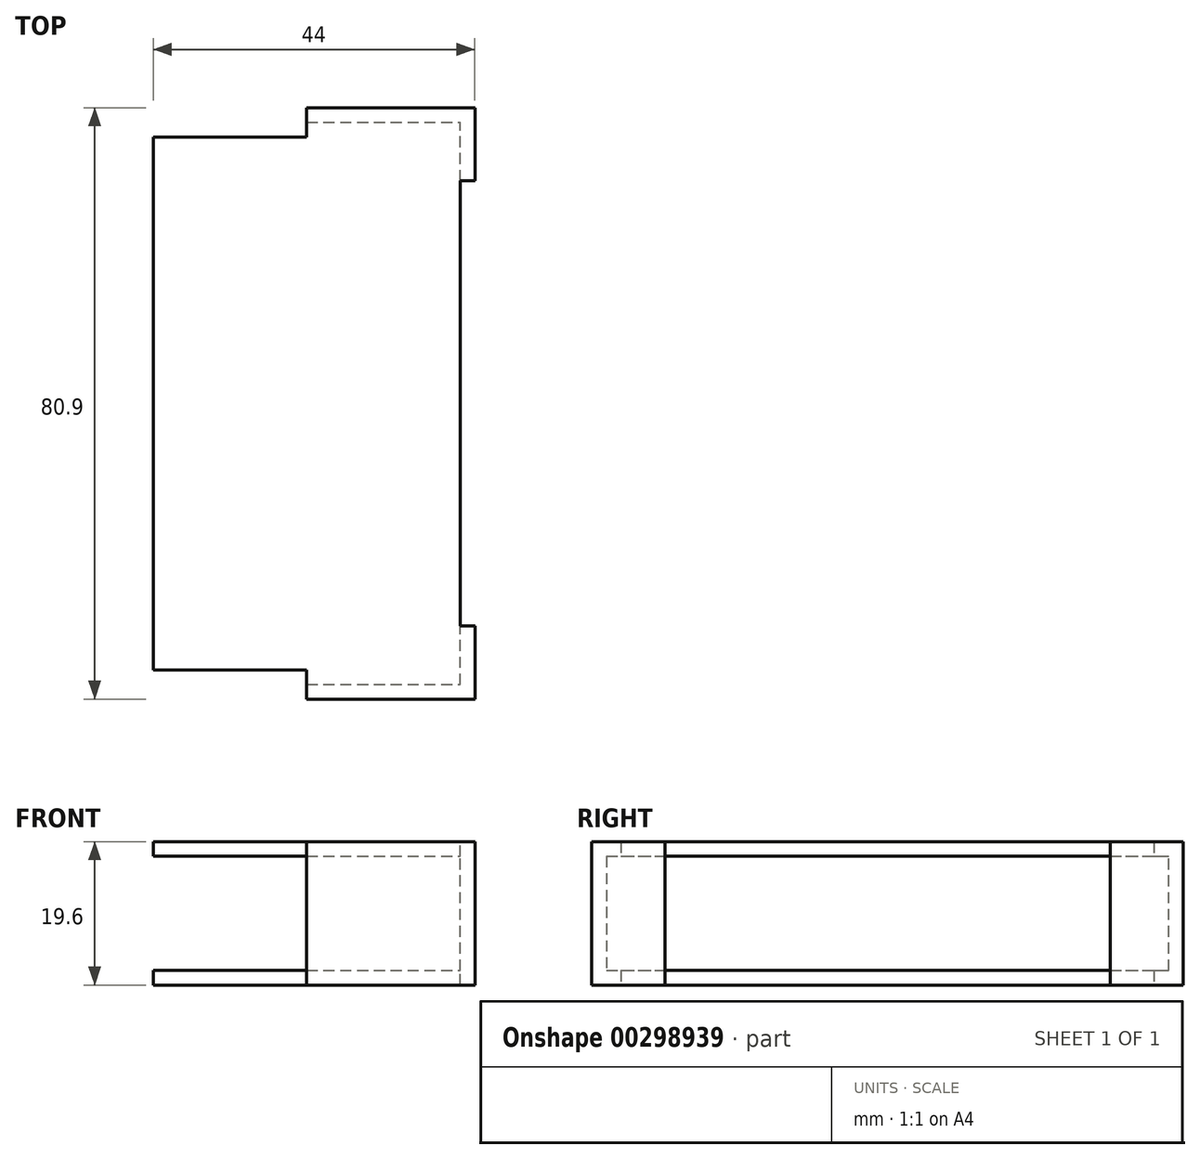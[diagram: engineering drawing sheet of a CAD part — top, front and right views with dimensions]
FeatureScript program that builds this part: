
annotation { "Feature Type Name" : "Feature", "Feature Type Description" : "" }
export const myFeature = defineFeature(function(context is Context, id is Id, definition is map)
    precondition{}
    {
        {
            var Q0;
            Q0=qCreatedBy(makeId("Front.planeOp"),FACE);
            var sketch = newSketch(context, id + "F0", { "sketchPlane" : qUnion([Q0])});
            skLineSegment(sketch, "E0.bottom", {"start": v(-6.87, 0) * mm, "end": v(11.13, 0) * mm});
            skLineSegment(sketch, "E0.top", {"start": v(-6.87, 15.6) * mm, "end": v(11.13, 15.6) * mm});
            skLineSegment(sketch, "E0.left", {"start": v(-6.87, 0) * mm, "end": v(-6.87, 15.6) * mm});
            skLineSegment(sketch, "E0.right", {"start": v(11.13, 0) * mm, "end": v(11.13, 15.6) * mm});
            skLineSegment(sketch, "E1.top", {"start": v(-6.87, 17.6) * mm, "end": v(11.13, 17.6) * mm});
            skLineSegment(sketch, "E1.left", {"start": v(-6.87, 15.6) * mm, "end": v(-6.87, 17.6) * mm});
            skLineSegment(sketch, "E1.right", {"start": v(11.13, 15.6) * mm, "end": v(11.13, 17.6) * mm});
            skLineSegment(sketch, "E2.top", {"start": v(-6.87, -2) * mm, "end": v(11.13, -2) * mm});
            skLineSegment(sketch, "E2.left", {"start": v(-6.87, 0) * mm, "end": v(-6.87, -2) * mm});
            skLineSegment(sketch, "E2.right", {"start": v(11.13, 0) * mm, "end": v(11.13, -2) * mm});
            skSolve(sketch);
        }
        {
            var Q0;
            Q0 = qSketchRegion(id + "F0", true);
            extrude(context, id + "F1", {"entities" : qUnion([Q0]), "depth" : 2 * mm});
        }
        {
            var Q0;
            Q0=makeQuery(id+"F1.opExtrude","CAP_FACE",FACE,{"disambiguationData":[OSD([sQuery(id+"F0.wireOp",EDGE,"E0.left"),sQuery(id+"F0.wireOp",EDGE,"E0.right"),sQuery(id+"F0.wireOp",EDGE,"E1.top"),sQuery(id+"F0.wireOp",EDGE,"E1.left"),sQuery(id+"F0.wireOp",EDGE,"E1.right"),sQuery(id+"F0.wireOp",EDGE,"E2.top"),sQuery(id+"F0.wireOp",EDGE,"E2.left"),sQuery(id+"F0.wireOp",EDGE,"E2.right")])],"isStart":false});
            var sketch = newSketch(context, id + "F2", { "sketchPlane" : qUnion([Q0])});
            skLineSegment(sketch, "E3.0", {"start": v(-6.87, 15.6) * mm, "end": v(11.13, 15.6) * mm});
            skLineSegment(sketch, "E4.0", {"start": v(-6.87, 0) * mm, "end": v(11.13, 0) * mm});
            skLineSegment(sketch, "E5", {"start": v(11.13, 17.6) * mm, "end": v(11.13, 15.6) * mm});
            skLineSegment(sketch, "E6.bottom", {"start": v(-6.87, 17.6) * mm, "end": v(11.13, 17.6) * mm});
            skLineSegment(sketch, "E6.left", {"start": v(-6.87, 17.6) * mm, "end": v(-6.87, 15.6) * mm});
            skLineSegment(sketch, "E7.bottom", {"start": v(11.13, -2) * mm, "end": v(-6.87, -2) * mm});
            skLineSegment(sketch, "E7.top", {"start": v(11.13, 0) * mm, "end": v(-6.87, 0) * mm});
            skLineSegment(sketch, "E7.left", {"start": v(11.13, -2) * mm, "end": v(11.13, 0) * mm});
            skLineSegment(sketch, "E7.right", {"start": v(-6.87, -2) * mm, "end": v(-6.87, 0) * mm});
            skSolve(sketch);
        }
        {
            var Q0;
            Q0 = qSketchRegion(id + "F2", true);
            extrude(context, id + "F3", {"entities" : qUnion([Q0]), "operationType" : NewBodyOperationType.ADD, "depth" : 76.9 * mm});
        }
        {
            var Q0;
            Q0=makeQuery(id+"F3.opExtrude","CAP_FACE",FACE,{"disambiguationData":[OSD([sQuery(id+"F2.wireOp",EDGE,"E6.bottom"),sQuery(id+"F2.wireOp",EDGE,"E3.0"),sQuery(id+"F2.wireOp",EDGE,"E6.left"),sQuery(id+"F2.wireOp",EDGE,"E5")])],"isStart":false});
            var sketch = newSketch(context, id + "F4", { "sketchPlane" : qUnion([Q0])});
            skLineSegment(sketch, "E8.0", {"start": v(-6.87, -2) * mm, "end": v(11.13, -2) * mm});
            skLineSegment(sketch, "E9.bottom", {"start": v(-6.87, 17.6) * mm, "end": v(11.13, 17.6) * mm});
            skLineSegment(sketch, "E9.left", {"start": v(-6.87, 17.6) * mm, "end": v(-6.87, -2) * mm});
            skLineSegment(sketch, "E9.right", {"start": v(11.13, 17.6) * mm, "end": v(11.13, -2) * mm});
            skSolve(sketch);
        }
        {
            var Q0;
            Q0 = qSketchRegion(id + "F4", true);
            extrude(context, id + "F5", {"entities" : qUnion([Q0]), "operationType" : NewBodyOperationType.ADD, "depth" : 2 * mm});
        }
        {
            var Q0;
            Q0=makeQuery(id+"F5.boolean.opBoolean","MERGE",FACE,{"derivedFrom":[makeQuery(id+"F3.boolean.opBoolean","MERGE",FACE,{"derivedFrom":[makeQuery(id+"F1.opExtrude","SWEPT_FACE",FACE,{"disambiguationData":[OSD([sQuery(id+"F0.wireOp",EDGE,"E0.left"),sQuery(id+"F0.wireOp",EDGE,"E1.left"),sQuery(id+"F0.wireOp",EDGE,"E2.left")])]}),makeQuery(id+"F3.opExtrude","SWEPT_FACE",FACE,{"disambiguationData":[OSD([sQuery(id+"F2.wireOp",EDGE,"E6.left")])]}),makeQuery(id+"F3.opExtrude","SWEPT_FACE",FACE,{"disambiguationData":[OSD([sQuery(id+"F2.wireOp",EDGE,"E7.right")])]})]}),makeQuery(id+"F5.opExtrude","SWEPT_FACE",FACE,{"disambiguationData":[OSD([sQuery(id+"F4.wireOp",EDGE,"E9.left")])]})]});
            var sketch = newSketch(context, id + "F6", { "sketchPlane" : qUnion([Q0])});
            skLineSegment(sketch, "E10", {"start": v(0, 17.6) * mm, "end": v(4, 17.6) * mm});
            skLineSegment(sketch, "E11", {"start": v(4, 17.6) * mm, "end": v(4, 15.6) * mm});
            skLineSegment(sketch, "E12", {"start": v(80.9, 17.6) * mm, "end": v(76.9, 17.6) * mm});
            skLineSegment(sketch, "E13", {"start": v(76.9, 17.6) * mm, "end": v(76.9, 15.6) * mm});
            skLineSegment(sketch, "E14.bottom", {"start": v(76.9, 15.6) * mm, "end": v(4, 15.6) * mm});
            skLineSegment(sketch, "E14.top", {"start": v(76.9, 17.6) * mm, "end": v(4, 17.6) * mm});
            skLineSegment(sketch, "E14.left", {"start": v(76.9, 15.6) * mm, "end": v(76.9, 17.6) * mm});
            skLineSegment(sketch, "E14.right", {"start": v(4, 15.6) * mm, "end": v(4, 17.6) * mm});
            skLineSegment(sketch, "E15.bottom", {"start": v(4, 0) * mm, "end": v(76.9, 0) * mm});
            skLineSegment(sketch, "E15.top", {"start": v(4, -2) * mm, "end": v(76.9, -2) * mm});
            skLineSegment(sketch, "E15.left", {"start": v(4, 0) * mm, "end": v(4, -2) * mm});
            skLineSegment(sketch, "E15.right", {"start": v(76.9, 0) * mm, "end": v(76.9, -2) * mm});
            skSolve(sketch);
        }
        {
            var Q0;
            Q0 = qSketchRegion(id + "F6", true);
            extrude(context, id + "F7", {"entities" : qUnion([Q0]), "operationType" : NewBodyOperationType.ADD, "depth" : 21 * mm});
        }
        {
            var Q0;
            Q0=makeQuery(id+"F5.boolean.opBoolean","MERGE",FACE,{"derivedFrom":[makeQuery(id+"F3.boolean.opBoolean","MERGE",FACE,{"derivedFrom":[makeQuery(id+"F1.opExtrude","SWEPT_FACE",FACE,{"disambiguationData":[OSD([sQuery(id+"F0.wireOp",EDGE,"E0.right"),sQuery(id+"F0.wireOp",EDGE,"E1.right"),sQuery(id+"F0.wireOp",EDGE,"E2.right")])]}),makeQuery(id+"F3.opExtrude","SWEPT_FACE",FACE,{"disambiguationData":[OSD([sQuery(id+"F2.wireOp",EDGE,"E5")])]}),makeQuery(id+"F3.opExtrude","SWEPT_FACE",FACE,{"disambiguationData":[OSD([sQuery(id+"F2.wireOp",EDGE,"E7.left")])]})]}),makeQuery(id+"F5.opExtrude","SWEPT_FACE",FACE,{"disambiguationData":[OSD([sQuery(id+"F4.wireOp",EDGE,"E9.right")])]})]});
            var sketch = newSketch(context, id + "F8", { "sketchPlane" : qUnion([Q0])});
            skLineSegment(sketch, "E16.0.0", {"start": v(0, 17.6) * mm, "end": v(-80.9, 17.6) * mm});
            skLineSegment(sketch, "E16.0.1", {"start": v(-80.9, 17.6) * mm, "end": v(-80.9, -2) * mm});
            skLineSegment(sketch, "E16.0.2", {"start": v(-80.9, -2) * mm, "end": v(0, -2) * mm});
            skLineSegment(sketch, "E16.0.3", {"start": v(0, -2) * mm, "end": v(0, 17.6) * mm});
            skLineSegment(sketch, "E17.0", {"start": v(-78.9, 15.6) * mm, "end": v(-2, 15.6) * mm});
            skLineSegment(sketch, "E18.0", {"start": v(-78.9, 0) * mm, "end": v(-78.9, 15.6) * mm});
            skLineSegment(sketch, "E19.0", {"start": v(-78.9, 0) * mm, "end": v(-2, 0) * mm});
            skLineSegment(sketch, "E20.0", {"start": v(-2, 0) * mm, "end": v(-2, 15.6) * mm});
            skSolve(sketch);
        }
        {
            var Q0;
            Q0 = qSketchRegion(id + "F8", true);
            extrude(context, id + "F9", {"entities" : qUnion([Q0]), "operationType" : NewBodyOperationType.ADD, "depth" : 3 * mm});
        }
        {
            var Q0;
            Q0=makeQuery(id+"F9.opExtrude","CAP_FACE",FACE,{"disambiguationData":[OSD([sQuery(id+"F8.wireOp",EDGE,"E16.0.0"),sQuery(id+"F8.wireOp",EDGE,"E16.0.1"),sQuery(id+"F8.wireOp",EDGE,"E16.0.2"),sQuery(id+"F8.wireOp",EDGE,"E16.0.3"),sQuery(id+"F8.wireOp",EDGE,"E17.0"),sQuery(id+"F8.wireOp",EDGE,"E18.0"),sQuery(id+"F8.wireOp",EDGE,"E19.0"),sQuery(id+"F8.wireOp",EDGE,"E20.0")])],"isStart":false});
            var sketch = newSketch(context, id + "F10", { "sketchPlane" : qUnion([Q0])});
            skLineSegment(sketch, "E21.0", {"start": v(-78.9, 0) * mm, "end": v(-78.9, 15.6) * mm});
            skLineSegment(sketch, "E22.0", {"start": v(-80.9, -2) * mm, "end": v(-80.9, 17.6) * mm});
            skLineSegment(sketch, "E23", {"start": v(-78.9, 0) * mm, "end": v(-78.9, -2) * mm});
            skLineSegment(sketch, "E24.bottom", {"start": v(-78.9, -2) * mm, "end": v(-80.9, -2) * mm});
            skLineSegment(sketch, "E24.top", {"start": v(-78.9, 17.6) * mm, "end": v(-80.9, 17.6) * mm});
            skLineSegment(sketch, "E24.left", {"start": v(-78.9, -2) * mm, "end": v(-78.9, 17.6) * mm});
            skLineSegment(sketch, "E25.0", {"start": v(0, -2) * mm, "end": v(0, 17.6) * mm});
            skLineSegment(sketch, "E26", {"start": v(-2, 0) * mm, "end": v(-2, -2) * mm});
            skLineSegment(sketch, "E27.bottom", {"start": v(-2, -2) * mm, "end": v(0, -2) * mm});
            skLineSegment(sketch, "E27.top", {"start": v(-2, 17.6) * mm, "end": v(0, 17.6) * mm});
            skLineSegment(sketch, "E27.left", {"start": v(-2, -2) * mm, "end": v(-2, 17.6) * mm});
            skSolve(sketch);
        }
        {
            var Q0;
            Q0 = qSketchRegion(id + "F10", true);
            extrude(context, id + "F11", {"entities" : qUnion([Q0]), "operationType" : NewBodyOperationType.ADD, "depth" : 2 * mm});
        }
        {
            var Q0;
            Q0=makeQuery(id+"F11.boolean.opBoolean","MERGE",FACE,{"derivedFrom":[makeQuery(id+"F9.boolean.opBoolean","MERGE",FACE,{"derivedFrom":[makeQuery(id+"F5.opExtrude","CAP_FACE",FACE,{"disambiguationData":[OSD([sQuery(id+"F4.wireOp",EDGE,"E9.bottom"),sQuery(id+"F4.wireOp",EDGE,"E8.0"),sQuery(id+"F4.wireOp",EDGE,"E9.left"),sQuery(id+"F4.wireOp",EDGE,"E9.right")])],"isStart":true}),makeQuery(id+"F9.opExtrude","SWEPT_FACE",FACE,{"disambiguationData":[OSD([sQuery(id+"F8.wireOp",EDGE,"E18.0")])]})]}),makeQuery(id+"F11.opExtrude","SWEPT_FACE",FACE,{"disambiguationData":[OSD([sQuery(id+"F10.wireOp",EDGE,"E24.left")])]})]});
            var sketch = newSketch(context, id + "F12", { "sketchPlane" : qUnion([Q0])});
            skLineSegment(sketch, "E28.0", {"start": v(-16.13, -2) * mm, "end": v(-16.13, 17.6) * mm});
            skLineSegment(sketch, "E29.bottom", {"start": v(-14.13, -2) * mm, "end": v(-16.13, -2) * mm});
            skLineSegment(sketch, "E29.top", {"start": v(-14.13, 17.6) * mm, "end": v(-16.13, 17.6) * mm});
            skLineSegment(sketch, "E29.left", {"start": v(-14.13, -2) * mm, "end": v(-14.13, 17.6) * mm});
            skSolve(sketch);
        }
        {
            var Q0;
            Q0 = qSketchRegion(id + "F12", true);
            extrude(context, id + "F13", {"entities" : qUnion([Q0]), "operationType" : NewBodyOperationType.ADD, "depth" : 8 * mm});
        }
        {
            var Q0;
            Q0=makeQuery(id+"F11.boolean.opBoolean","MERGE",FACE,{"derivedFrom":[makeQuery(id+"F9.boolean.opBoolean","MERGE",FACE,{"derivedFrom":[makeQuery(id+"F1.opExtrude","CAP_FACE",FACE,{"disambiguationData":[OSD([sQuery(id+"F0.wireOp",EDGE,"E0.left"),sQuery(id+"F0.wireOp",EDGE,"E0.right"),sQuery(id+"F0.wireOp",EDGE,"E1.top"),sQuery(id+"F0.wireOp",EDGE,"E1.left"),sQuery(id+"F0.wireOp",EDGE,"E1.right"),sQuery(id+"F0.wireOp",EDGE,"E2.top"),sQuery(id+"F0.wireOp",EDGE,"E2.left"),sQuery(id+"F0.wireOp",EDGE,"E2.right")])],"isStart":false}),makeQuery(id+"F9.opExtrude","SWEPT_FACE",FACE,{"disambiguationData":[OSD([sQuery(id+"F8.wireOp",EDGE,"E20.0")])]})]}),makeQuery(id+"F11.opExtrude","SWEPT_FACE",FACE,{"disambiguationData":[OSD([sQuery(id+"F10.wireOp",EDGE,"E27.left")])]})]});
            var sketch = newSketch(context, id + "F14", { "sketchPlane" : qUnion([Q0])});
            skLineSegment(sketch, "E30.0", {"start": v(16.13, -2) * mm, "end": v(16.13, 17.6) * mm});
            skLineSegment(sketch, "E31.bottom", {"start": v(14.13, -2) * mm, "end": v(16.13, -2) * mm});
            skLineSegment(sketch, "E31.top", {"start": v(14.13, 17.6) * mm, "end": v(16.13, 17.6) * mm});
            skLineSegment(sketch, "E31.left", {"start": v(14.13, -2) * mm, "end": v(14.13, 17.6) * mm});
            skSolve(sketch);
        }
        {
            var Q0;
            Q0 = qSketchRegion(id + "F14", true);
            extrude(context, id + "F15", {"entities" : qUnion([Q0]), "operationType" : NewBodyOperationType.ADD, "depth" : 8 * mm});
        }
    });
